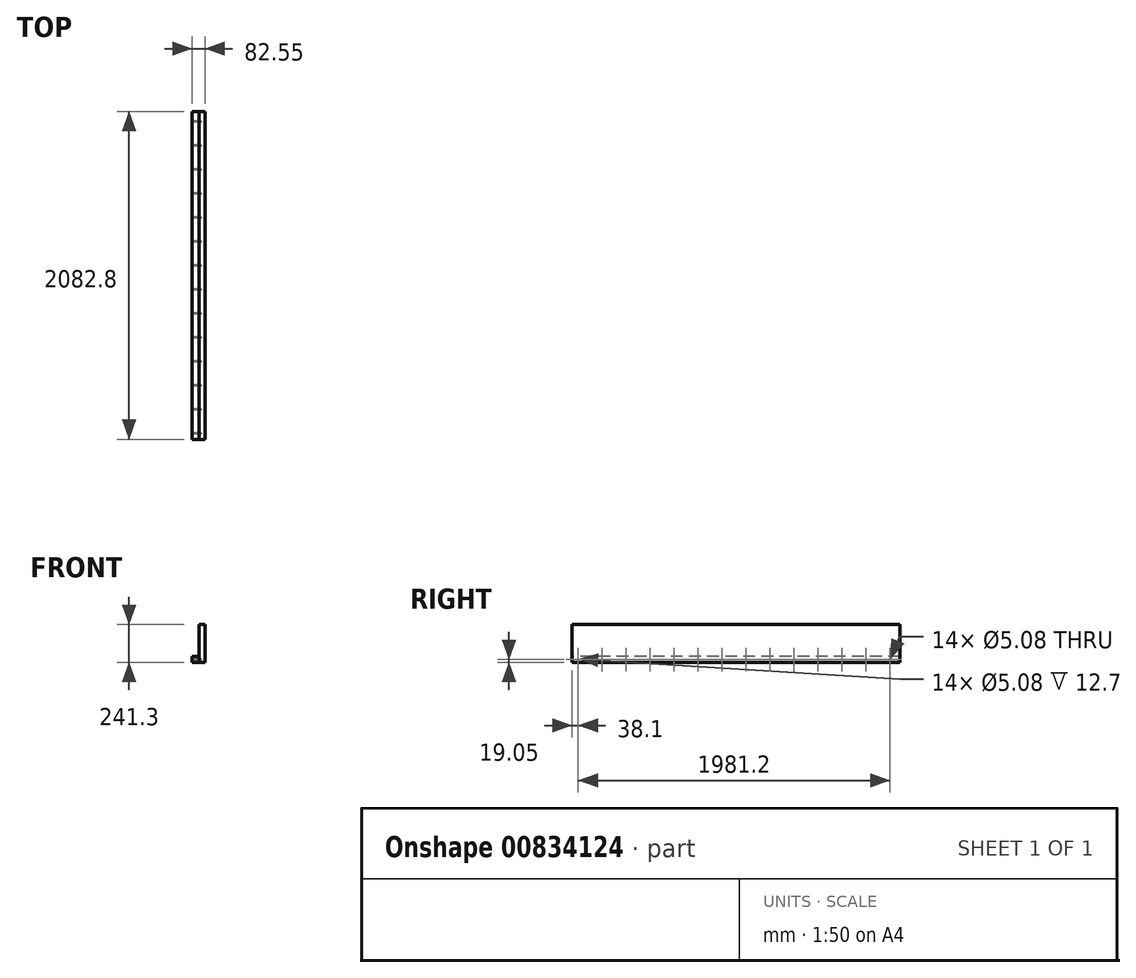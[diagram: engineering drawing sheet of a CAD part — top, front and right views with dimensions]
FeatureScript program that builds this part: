
annotation { "Feature Type Name" : "Feature", "Feature Type Description" : "" }
export const myFeature = defineFeature(function(context is Context, id is Id, definition is map)
    precondition{}
    {
        {
            var Q0;
            Q0=qCreatedBy(makeId("Right.planeOp"),FACE);
            var sketch = newSketch(context, id + "F0", { "sketchPlane" : qUnion([Q0])});
            skLineSegment(sketch, "E0.rect.bottom", {"start": v(-1041.4, 120.65) * mm, "end": v(1041.4, 120.65) * mm});
            skLineSegment(sketch, "E0.rect.top", {"start": v(-1041.4, -120.65) * mm, "end": v(1041.4, -120.65) * mm});
            skLineSegment(sketch, "E0.rect.left", {"start": v(-1041.4, 120.65) * mm, "end": v(-1041.4, -120.65) * mm});
            skLineSegment(sketch, "E0.rect.right", {"start": v(1041.4, 120.65) * mm, "end": v(1041.4, -120.65) * mm});
            skPoint(sketch, "E0.rect.middle", {"position": v(0, 0) * mm});
            skSolve(sketch);
        }
        {
            var Q0;
            Q0=qSketchRegion(id+"F0",true);
            extrude(context, id + "F1", {"entities" : qUnion([Q0]), "depth" : 38.1 * mm});
        }
        {
            var Q0;
            Q0=makeQuery(id+"F1.opExtrude","CAP_FACE",FACE,{"disambiguationData":[OSD([sQuery(id+"F0.wireOp",EDGE,"E0.rect.bottom"),sQuery(id+"F0.wireOp",EDGE,"E0.rect.top"),sQuery(id+"F0.wireOp",EDGE,"E0.rect.left"),sQuery(id+"F0.wireOp",EDGE,"E0.rect.right")])],"isStart":true});
            var sketch = newSketch(context, id + "F2", { "sketchPlane" : qUnion([Q0])});
            skLineSegment(sketch, "E1.bottom", {"start": v(-1041.4, -82.55) * mm, "end": v(1041.4, -82.55) * mm});
            skLineSegment(sketch, "E1.top", {"start": v(-1041.4, -120.65) * mm, "end": v(1041.4, -120.65) * mm});
            skLineSegment(sketch, "E1.left", {"start": v(-1041.4, -82.55) * mm, "end": v(-1041.4, -120.65) * mm});
            skLineSegment(sketch, "E1.right", {"start": v(1041.4, -82.55) * mm, "end": v(1041.4, -120.65) * mm});
            skSolve(sketch);
        }
        {
            var Q0;
            Q0=qSketchRegion(id+"F2",true);
            extrude(context, id + "F3", {"entities" : qUnion([Q0]), "depth" : 44.45 * mm});
        }
        {
            var Q0;
            Q0=makeQuery(id+"F3.opExtrude","CAP_FACE",FACE,{"disambiguationData":[OSD([sQuery(id+"F2.wireOp",EDGE,"E1.bottom"),sQuery(id+"F2.wireOp",EDGE,"E1.top"),sQuery(id+"F2.wireOp",EDGE,"E1.left"),sQuery(id+"F2.wireOp",EDGE,"E1.right")])],"isStart":false});
            var sketch = newSketch(context, id + "F4", { "sketchPlane" : qUnion([Q0])});
            skCircle(sketch, "E2", {"center": v(1003.3, -101.6) * mm, "radius": 2.54 * mm});
            skLineSegment(sketch, "E3", {"start": v(1041.4, -101.6) * mm, "end": v(1003.3, -101.6) * mm, "construction": true});
            skCircle(sketch, "E4.1.0.0", {"center": v(850.9, -101.6) * mm, "radius": 2.54 * mm});
            skCircle(sketch, "E4.2.0.0", {"center": v(698.5, -101.6) * mm, "radius": 2.54 * mm});
            skCircle(sketch, "E4.3.0.0", {"center": v(546.1, -101.6) * mm, "radius": 2.54 * mm});
            skCircle(sketch, "E4.4.0.0", {"center": v(393.7, -101.6) * mm, "radius": 2.54 * mm});
            skCircle(sketch, "E4.5.0.0", {"center": v(241.3, -101.6) * mm, "radius": 2.54 * mm});
            skCircle(sketch, "E4.6.0.0", {"center": v(88.9, -101.6) * mm, "radius": 2.54 * mm});
            skCircle(sketch, "E4.7.0.0", {"center": v(-63.5, -101.6) * mm, "radius": 2.54 * mm});
            skCircle(sketch, "E4.8.0.0", {"center": v(-215.9, -101.6) * mm, "radius": 2.54 * mm});
            skCircle(sketch, "E4.9.0.0", {"center": v(-368.3, -101.6) * mm, "radius": 2.54 * mm});
            skCircle(sketch, "E4.10.0.0", {"center": v(-520.7, -101.6) * mm, "radius": 2.54 * mm});
            skCircle(sketch, "E4.11.0.0", {"center": v(-673.1, -101.6) * mm, "radius": 2.54 * mm});
            skCircle(sketch, "E4.12.0.0", {"center": v(-825.5, -101.6) * mm, "radius": 2.54 * mm});
            skCircle(sketch, "E4.13.0.0", {"center": v(-977.9, -101.6) * mm, "radius": 2.54 * mm});
            skLineSegment(sketch, "E4.direction1", {"start": v(1003.3, -101.6) * mm, "end": v(850.9, -101.6) * mm, "construction": true});
            skSolve(sketch);
        }
        {
            var Q0;
            Q0=qSketchRegion(id+"F4",true);
            extrude(context, id + "F5", {"entities" : qUnion([Q0]), "operationType" : NewBodyOperationType.REMOVE, "oppositeDirection" : true, "depth" : 57.15 * mm});
        }
    });
